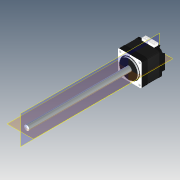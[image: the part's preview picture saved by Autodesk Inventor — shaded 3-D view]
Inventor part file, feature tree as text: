
AUTODESK INVENTOR PART (.ipt)
format: ipt  version: 2022 (Build 260153000, 153)  size: 192,000 bytes
history: imported  units: in
note: dims shown in document units (in); Inventor stores cm internally (conversion verified against a paired STEP export)
features: plane x2, other x1, imported_body x1
ambient origin geometry x8: Origin, YZ Plane, XZ Plane, XY Plane, X Axis, Y Axis, Z Axis, Center Point
bodies: Solid1 (imported_parasolid)
feature tree (4):
  other  "Shaft"
  plane  "Arbeitsebene1"
  plane  "Arbeitsebene2"
  imported_body  NMx_Import_Brep_tag  [imported B-rep: ~112 faces, bbox_mm=[28.5, 31.2, 151.0]]
